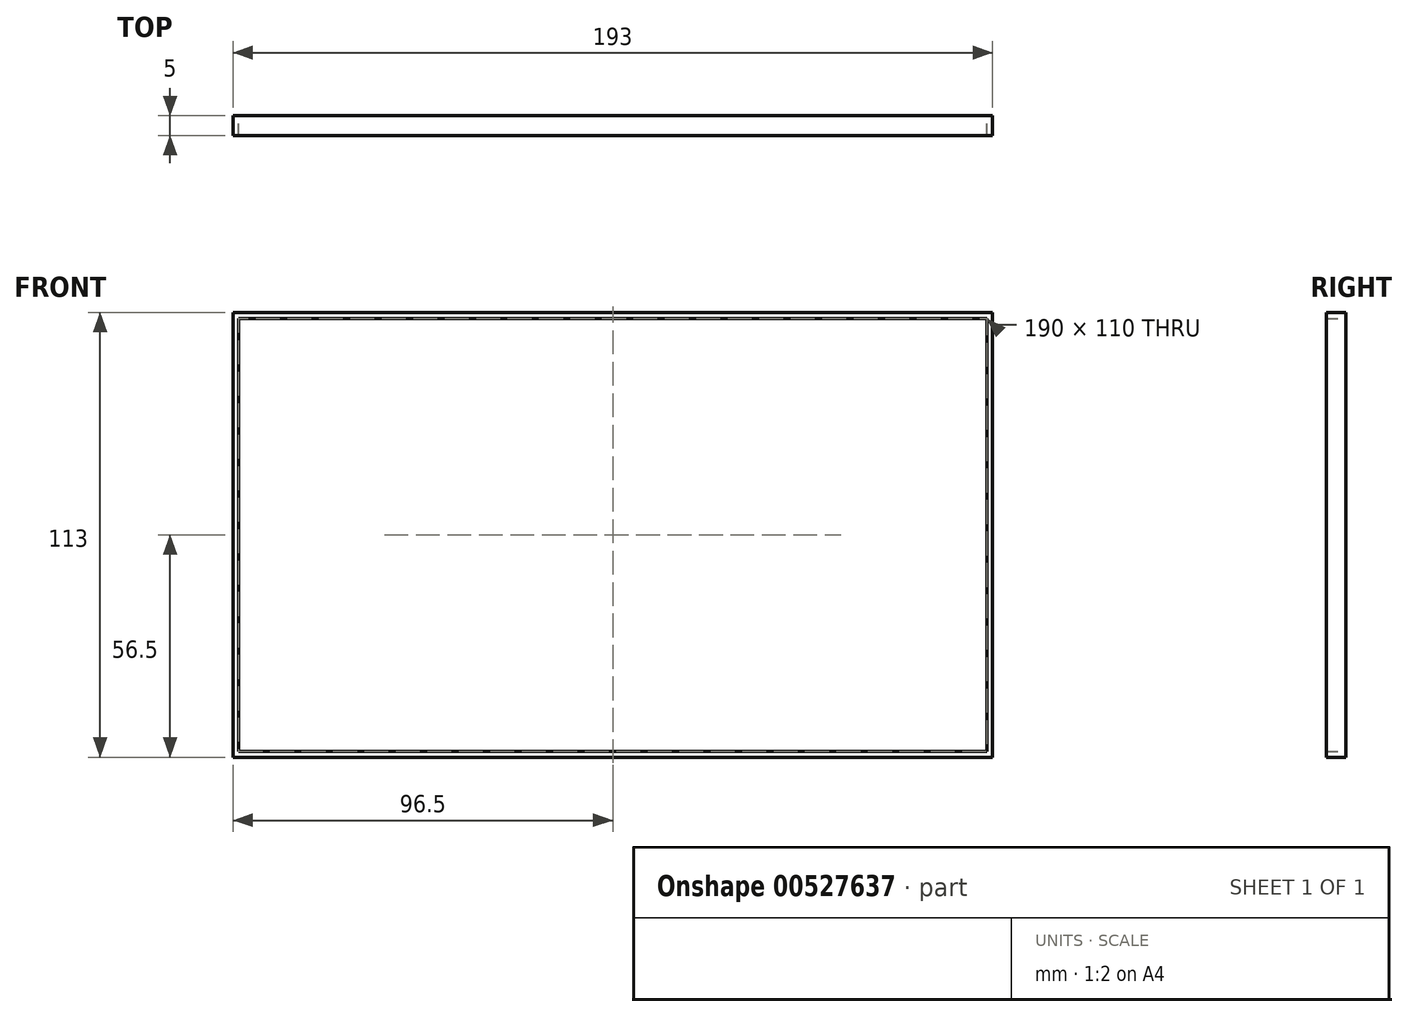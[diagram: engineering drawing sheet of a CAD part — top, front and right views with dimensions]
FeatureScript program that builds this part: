
annotation { "Feature Type Name" : "Feature", "Feature Type Description" : "" }
export const myFeature = defineFeature(function(context is Context, id is Id, definition is map)
    precondition{}
    {
        {
            var Q0;
            Q0=qCreatedBy(makeId("Front.planeOp"),FACE);
            var sketch = newSketch(context, id + "F0", { "sketchPlane" : qUnion([Q0])});
            skLineSegment(sketch, "E0.bottom", {"start": v(96.5, -56.5) * mm, "end": v(-96.5, -56.5) * mm});
            skLineSegment(sketch, "E0.top", {"start": v(96.5, 56.5) * mm, "end": v(-96.5, 56.5) * mm});
            skLineSegment(sketch, "E0.left", {"start": v(96.5, -56.5) * mm, "end": v(96.5, 56.5) * mm});
            skLineSegment(sketch, "E0.right", {"start": v(-96.5, -56.5) * mm, "end": v(-96.5, 56.5) * mm});
            skPoint(sketch, "E0.middle", {"position": v(0, 0) * mm});
            skLineSegment(sketch, "E1.bottom", {"start": v(95, -55) * mm, "end": v(-95, -55) * mm});
            skLineSegment(sketch, "E1.top", {"start": v(95, 55) * mm, "end": v(-95, 55) * mm});
            skLineSegment(sketch, "E1.left", {"start": v(95, -55) * mm, "end": v(95, 55) * mm});
            skLineSegment(sketch, "E1.right", {"start": v(-95, -55) * mm, "end": v(-95, 55) * mm});
            skSolve(sketch);
        }
        {
            var Q0;
            Q0 = qSketchRegion(id + "F0", true);
            extrude(context, id + "F1", {"entities" : qUnion([Q0]), "depth" : 5 * mm, "offsetDistance" : 25 * mm});
        }
    });
